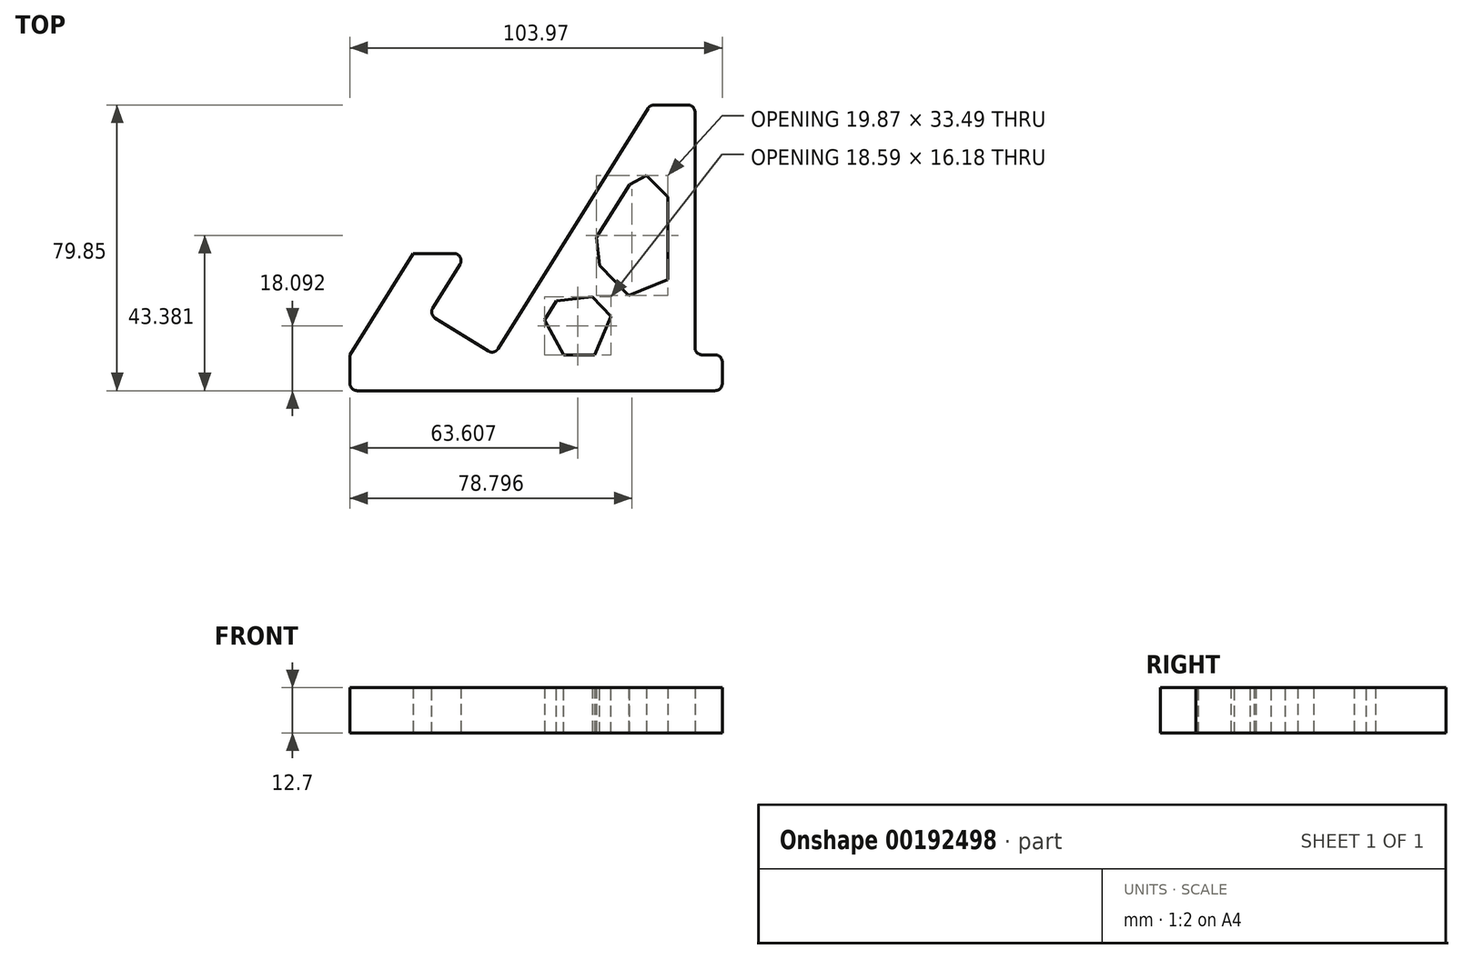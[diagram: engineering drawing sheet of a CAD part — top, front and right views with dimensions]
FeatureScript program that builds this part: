
annotation { "Feature Type Name" : "Feature", "Feature Type Description" : "" }
export const myFeature = defineFeature(function(context is Context, id is Id, definition is map)
    precondition{}
    {
        {
            var Q0;
            Q0=qCreatedBy(makeId("Top.planeOp"),FACE);
            var sketch = newSketch(context, id + "F0", { "sketchPlane" : qUnion([Q0])});
            skLineSegment(sketch, "E0", {"start": v(0, 0) * mm, "end": v(17.66, 28.34) * mm});
            skLineSegment(sketch, "E1", {"start": v(17.66, 28.34) * mm, "end": v(32.66, 28.34) * mm});
            skLineSegment(sketch, "E2", {"start": v(32.66, 28.34) * mm, "end": v(22.08, 11.37) * mm});
            skLineSegment(sketch, "E3", {"start": v(22.08, 11.37) * mm, "end": v(40.33, 0) * mm});
            skLineSegment(sketch, "E4", {"start": v(40.33, 0) * mm, "end": v(83.85, 69.85) * mm});
            skLineSegment(sketch, "E5", {"start": v(83.85, 69.85) * mm, "end": v(96.35, 69.85) * mm});
            skLineSegment(sketch, "E6", {"start": v(96.35, 69.85) * mm, "end": v(96.35, 0) * mm});
            skLineSegment(sketch, "E7", {"start": v(0, 0) * mm, "end": v(0, -10) * mm});
            skLineSegment(sketch, "E8", {"start": v(0, -10) * mm, "end": v(103.97, -10) * mm});
            skLineSegment(sketch, "E9", {"start": v(103.97, -10) * mm, "end": v(103.97, 0) * mm});
            skLineSegment(sketch, "E10", {"start": v(103.97, 0) * mm, "end": v(96.35, 0) * mm});
            skLineSegment(sketch, "E11", {"start": v(0, 0) * mm, "end": v(96.35, 0) * mm, "construction": true});
            skLineSegment(sketch, "E12", {"start": v(48.18, 0) * mm, "end": v(80.03, 50.53) * mm});
            skLineSegment(sketch, "E13", {"start": v(80.03, 50.53) * mm, "end": v(88.73, 50.53) * mm});
            skLineSegment(sketch, "E14", {"start": v(88.73, 50.53) * mm, "end": v(88.73, 0) * mm});
            skLineSegment(sketch, "E15", {"start": v(88.73, 0) * mm, "end": v(48.18, 0) * mm});
            skLineSegment(sketch, "E16", {"start": v(88.73, 0) * mm, "end": v(64.1, 25.27) * mm, "construction": true});
            skLineSegment(sketch, "E17", {"start": v(66.2, 28.58) * mm, "end": v(88.73, 5.46) * mm});
            skLineSegment(sketch, "E18", {"start": v(83.41, 0) * mm, "end": v(62.01, 21.95) * mm});
            skSolve(sketch);
        }
        {
            var Q0;
            Q0=makeQuery(id+"F0.imprint","IMPRINT",FACE,{"disambiguationData":[TD([[makeQuery(id+"F0.imprint","IMPRINT",EDGE,{"derivedFrom":sQuery(id+"F0.wireOp",EDGE,"E0")}),-1.0]])]});
            var Q1;
            Q1=makeQuery(id+"F0.imprint","IMPRINT",FACE,{"disambiguationData":[TD([[makeQuery(id+"F0.imprint","IMPRINT",EDGE,{"derivedFrom":sQuery(id+"F0.wireOp",EDGE,"8cc8dda4-1ff4-42f5-a2e3-02bb7101f472")}),1.0]])]});
            var Q2;
            {var subQ0=sQuery(id+"F0.wireOp",EDGE,"E17");Q2=makeQuery(id+"F0.imprint","IMPRINT",FACE,{"disambiguationData":[TD([[makeQuery(id+"F0.imprint","IMPRINT",EDGE,{"derivedFrom":subQ0}),-1.0]])]});}
            extrude(context, id + "F1", {"entities" : qUnion([Q0, Q1, Q2]), "offsetDistance" : 25.4 * mm, "depth" : 12.7 * mm});
        }
        {
            var Q0;
            Q0=makeQuery(id+"F1.opExtrude","SWEPT_EDGE",EDGE,{"disambiguationData":[OSD([sQuery(id+"F0.wireOp",EDGE,"E1"),sQuery(id+"F0.wireOp",EDGE,"E2")])]});
            var Q1;
            Q1=makeQuery(id+"F1.opExtrude","SWEPT_EDGE",EDGE,{"disambiguationData":[OSD([sQuery(id+"F0.wireOp",EDGE,"E5"),sQuery(id+"F0.wireOp",EDGE,"E6")])]});
            var Q2;
            Q2=makeQuery(id+"F1.opExtrude","SWEPT_EDGE",EDGE,{"disambiguationData":[OSD([sQuery(id+"F0.wireOp",EDGE,"E4"),sQuery(id+"F0.wireOp",EDGE,"E5")])]});
            var Q3;
            Q3=makeQuery(id+"F1.opExtrude","SWEPT_EDGE",EDGE,{"disambiguationData":[OSD([sQuery(id+"F0.wireOp",EDGE,"E9"),sQuery(id+"F0.wireOp",EDGE,"E10")])]});
            var Q4;
            Q4=makeQuery(id+"F1.opExtrude","SWEPT_EDGE",EDGE,{"disambiguationData":[OSD([sQuery(id+"F0.wireOp",EDGE,"PochhMeM-2wws-lU01-S2kx-9X6qScFzxdY0"),sQuery(id+"F0.wireOp",EDGE,"Ddw032Rd-OZUl-DPwW-q0VL-ZR035MvSg6z7")])]});
            var Q5;
            Q5=makeQuery(id+"F1.opExtrude","SWEPT_EDGE",EDGE,{"disambiguationData":[OSD([sQuery(id+"F0.wireOp",EDGE,"PochhMeM-2wws-lU01-S2kx-9X6qScFzxdY0"),sQuery(id+"F0.wireOp",EDGE,"VrdRBgX9-rTGt-gVhE-JREq-3jjhgnSfDI1U")])]});
            var Q6;
            Q6=makeQuery(id+"F1.opExtrude","SWEPT_EDGE",EDGE,{"disambiguationData":[OSD([sQuery(id+"F0.wireOp",EDGE,"Ddw032Rd-OZUl-DPwW-q0VL-ZR035MvSg6z7"),sQuery(id+"F0.wireOp",EDGE,"VrdRBgX9-rTGt-gVhE-JREq-3jjhgnSfDI1U")])]});
            var Q7;
            Q7=makeQuery(id+"F1.opExtrude","SWEPT_EDGE",EDGE,{"disambiguationData":[OSD([sQuery(id+"F0.wireOp",EDGE,"ItXIaZwX-PzH9-taSW-UR8Z-8fym72IKNTmN"),sQuery(id+"F0.wireOp",EDGE,"rhLaobgN-rVpL-HgFP-mrio-eAa5aLfcsOgb")])]});
            var Q8;
            Q8=makeQuery(id+"F1.opExtrude","SWEPT_EDGE",EDGE,{"disambiguationData":[OSD([sQuery(id+"F0.wireOp",EDGE,"ItXIaZwX-PzH9-taSW-UR8Z-8fym72IKNTmN"),sQuery(id+"F0.wireOp",EDGE,"5gaUlG2U-CDfC-fejA-4pzM-ZeyNVRoPlXpJ")])]});
            var Q9;
            Q9=makeQuery(id+"F1.opExtrude","SWEPT_EDGE",EDGE,{"disambiguationData":[OSD([sQuery(id+"F0.wireOp",EDGE,"rhLaobgN-rVpL-HgFP-mrio-eAa5aLfcsOgb"),sQuery(id+"F0.wireOp",EDGE,"5gaUlG2U-CDfC-fejA-4pzM-ZeyNVRoPlXpJ")])]});
            var Q10;
            Q10=makeQuery(id+"F1.opExtrude","SWEPT_EDGE",EDGE,{"disambiguationData":[OSD([sQuery(id+"F0.wireOp",EDGE,"cbbt0EHP-K1FU-sEri-tuhG-MRDXMNq4uWD7"),sQuery(id+"F0.wireOp",EDGE,"5yEPmZHD-kp3t-uyLL-TT40-IGWi4ntT41bW")])]});
            var Q11;
            Q11=makeQuery(id+"F1.opExtrude","SWEPT_EDGE",EDGE,{"disambiguationData":[OSD([sQuery(id+"F0.wireOp",EDGE,"E2"),sQuery(id+"F0.wireOp",EDGE,"E3")])]});
            var Q12;
            Q12=makeQuery(id+"F1.opExtrude","SWEPT_EDGE",EDGE,{"disambiguationData":[OSD([sQuery(id+"F0.wireOp",EDGE,"E3"),sQuery(id+"F0.wireOp",EDGE,"E4")])]});
            var Q13;
            Q13=makeQuery(id+"F1.opExtrude","SWEPT_EDGE",EDGE,{"disambiguationData":[OSD([sQuery(id+"F0.wireOp",EDGE,"E6"),sQuery(id+"F0.wireOp",EDGE,"E10")])]});
            var Q14;
            Q14=makeQuery(id+"F1.opExtrude","SWEPT_EDGE",EDGE,{"disambiguationData":[OSD([sQuery(id+"F0.wireOp",EDGE,"E7"),sQuery(id+"F0.wireOp",EDGE,"E8")])]});
            var Q15;
            Q15=makeQuery(id+"F1.opExtrude","SWEPT_EDGE",EDGE,{"disambiguationData":[OSD([sQuery(id+"F0.wireOp",EDGE,"E8"),sQuery(id+"F0.wireOp",EDGE,"E9")])]});
            fillet(context, id + "F2", {"entities" : qUnion([Q0, Q1, Q2, Q3, Q4, Q5, Q6, Q7, Q8, Q9, Q10, Q11, Q12, Q13, Q14, Q15]), "radius" : 2 * mm, "tangentPropagation" : true, "allowEdgeOverflow" : false});
        }
        {
            var Q0;
            Q0=makeQuery(id+"F1.opExtrude","SWEPT_EDGE",EDGE,{"disambiguationData":[OSD([sQuery(id+"F0.wireOp",EDGE,"E12"),sQuery(id+"F0.wireOp",EDGE,"E15")])]});
            var Q1;
            Q1=makeQuery(id+"F1.opExtrude","SWEPT_EDGE",EDGE,{"disambiguationData":[OSD([sQuery(id+"F0.wireOp",EDGE,"E12"),sQuery(id+"F0.wireOp",EDGE,"E18")])]});
            var Q2;
            Q2=makeQuery(id+"F1.opExtrude","SWEPT_EDGE",EDGE,{"disambiguationData":[OSD([sQuery(id+"F0.wireOp",EDGE,"E12"),sQuery(id+"F0.wireOp",EDGE,"E17")])]});
            var Q3;
            Q3=makeQuery(id+"F1.opExtrude","SWEPT_EDGE",EDGE,{"disambiguationData":[OSD([sQuery(id+"F0.wireOp",EDGE,"E14"),sQuery(id+"F0.wireOp",EDGE,"E17")])]});
            var Q4;
            Q4=makeQuery(id+"F1.opExtrude","SWEPT_EDGE",EDGE,{"disambiguationData":[OSD([sQuery(id+"F0.wireOp",EDGE,"E15"),sQuery(id+"F0.wireOp",EDGE,"E18")])]});
            var Q5;
            Q5=makeQuery(id+"F1.opExtrude","SWEPT_EDGE",EDGE,{"disambiguationData":[OSD([sQuery(id+"F0.wireOp",EDGE,"E13"),sQuery(id+"F0.wireOp",EDGE,"E14")])]});
            var Q6;
            Q6=makeQuery(id+"F1.opExtrude","SWEPT_EDGE",EDGE,{"disambiguationData":[OSD([sQuery(id+"F0.wireOp",EDGE,"E12"),sQuery(id+"F0.wireOp",EDGE,"E13")])]});
            chamfer(context, id + "F3", {"entities" : qUnion([Q0, Q1, Q2, Q3, Q4, Q5, Q6]), "width" : 6.35 * mm, "tangentPropagation" : true});
        }
    });
